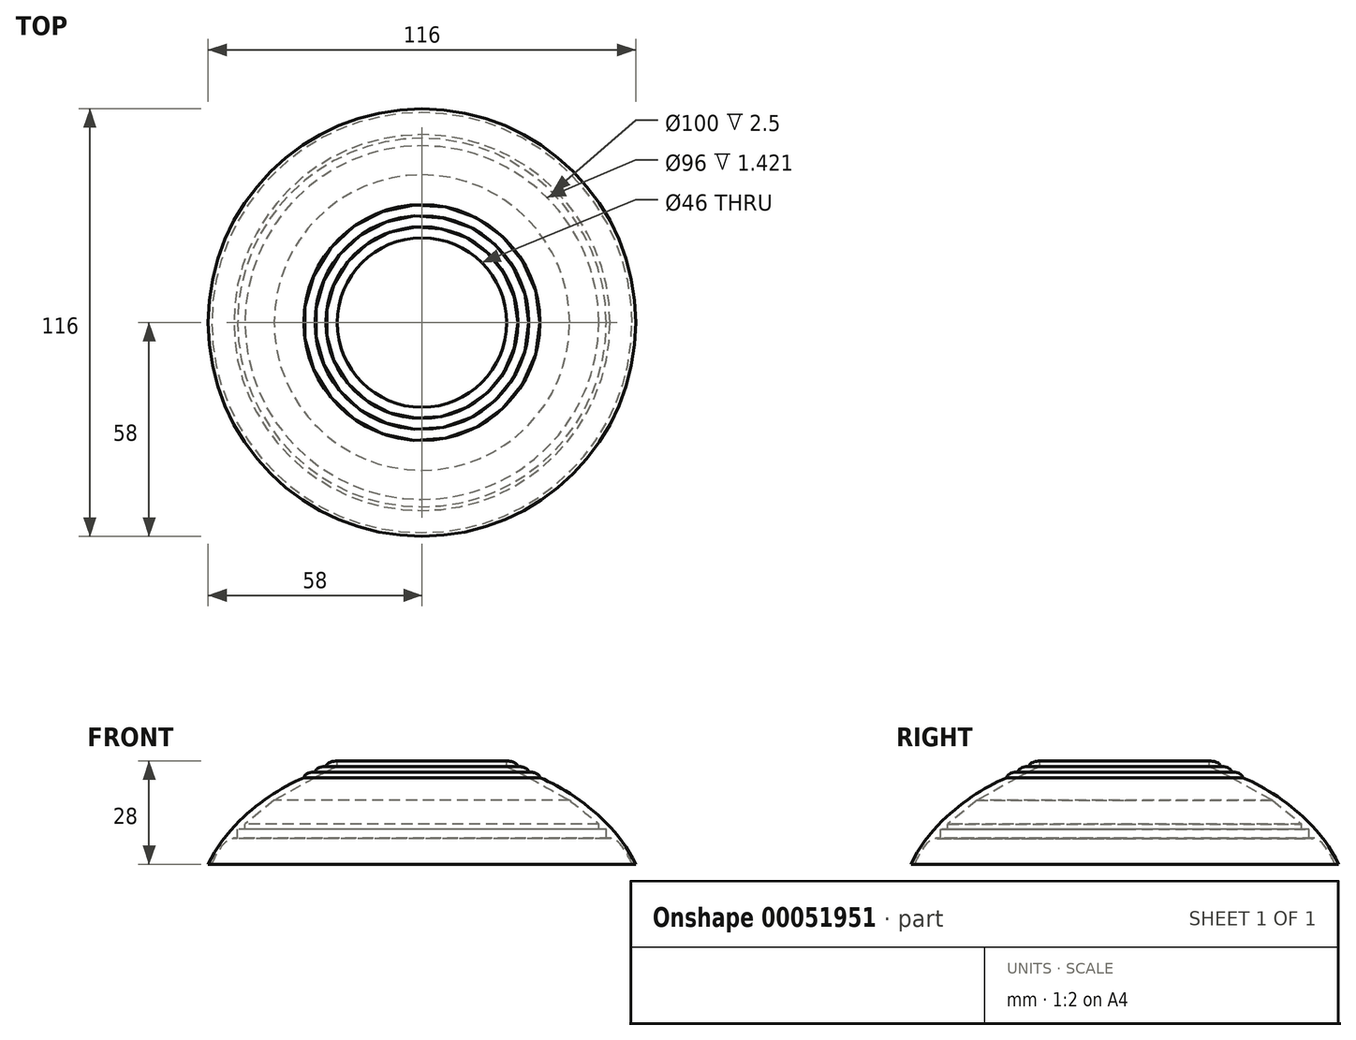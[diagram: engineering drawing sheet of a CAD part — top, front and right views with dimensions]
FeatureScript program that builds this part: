
annotation { "Feature Type Name" : "Feature", "Feature Type Description" : "" }
export const myFeature = defineFeature(function(context is Context, id is Id, definition is map)
    precondition{}
    {
        {
            var Q0;
            Q0=qCreatedBy(makeId("Front.planeOp"),FACE);
            var sketch = newSketch(context, id + "F0", { "sketchPlane" : qUnion([Q0])});
            skEllipticalArc(sketch, "E0.1.0.0", {});
            skEllipticalArc(sketch, "E0.2.0.0", {});
            skFitSpline(sketch, "E1", {"points": [v(-32, 23.5) * mm, v(-44.67, 15.96) * mm, v(-58, 0) * mm], "startDerivative": vector(-24.72, -10.42) * mm, "endDerivative": vector(-18.15, -37.78) * mm});
            skLineSegment(sketch, "E2", {"start": v(-23, 28) * mm, "end": v(-23, 26.5) * mm});
            skEllipticalArc(sketch, "E3.trimOffspring", {});
            skLineSegment(sketch, "E4", {"start": v(-50, 7) * mm, "end": v(-50, 9.5) * mm});
            skLineSegment(sketch, "E5", {"start": v(-50, 9.5) * mm, "end": v(-48, 9.5) * mm});
            skLineSegment(sketch, "E6", {"start": v(-48, 9.5) * mm, "end": v(-48, 10.92) * mm});
            skLineSegment(sketch, "E7", {"start": v(-58, 0) * mm, "end": v(-57, 0) * mm});
            skFitSpline(sketch, "E8", {"points": [v(-57.1, -0.27) * mm, v(-52.46, 6.6) * mm, v(-49.83, 5.1) * mm], "startDerivative": vector(3.42, 8.89) * mm, "endDerivative": vector(1, -16.64) * mm});
            skLineSegment(sketch, "E9.trimOffspring", {"start": v(-51.01, 7) * mm, "end": v(-50, 7) * mm});
            skLineSegment(sketch, "E10", {"start": v(-48, 10.92) * mm, "end": v(-40.1, 17.3) * mm});
            skLineSegment(sketch, "E11", {"start": v(-40.1, 17.3) * mm, "end": v(-29.01, 23.5) * mm});
            skLineSegment(sketch, "E12", {"start": v(-29.01, 23.5) * mm, "end": v(-26.03, 25) * mm});
            skLineSegment(sketch, "E13", {"start": v(-26.03, 25) * mm, "end": v(-23, 26.5) * mm});
            skLineSegment(sketch, "E14", {"start": v(0, 45.89) * mm, "end": v(0, -32.25) * mm, "construction": true});
            const initialGuessF0  = {"E0.1.0.0": [-0.026025703176857387, 0.025, 1, 0, 0.0029742968231425966, 0.0015000560132257012, 1.5621544533317187, 3.1415926535897922], "E0.2.0.0": [-0.029010102460748467, 0.0235, 1, 0, 0.002989897539251519, 0.0015000085626208518, 1.5674174551650844, 3.1415926535897927], "E3.trimOffspring": [-0.023, 0.0265, 1, 0, 0.003, 0.0015, 1.5707963267948963, 3.1415926535897927]};
            skSetInitialGuess(sketch, initialGuessF0);
            skSolve(sketch);
        }
        {
            var Q0;
            Q0 = qSketchRegion(id + "F0", true);
            var Q1;
            Q1=sQuery(id+"F0.wireOp",EDGE,"E14");
            revolve(context, id + "F1", {"entities" : qUnion([Q0]), "axis" : qUnion([Q1]), "revolveType" : RevolveType.FULL});
        }
    });
